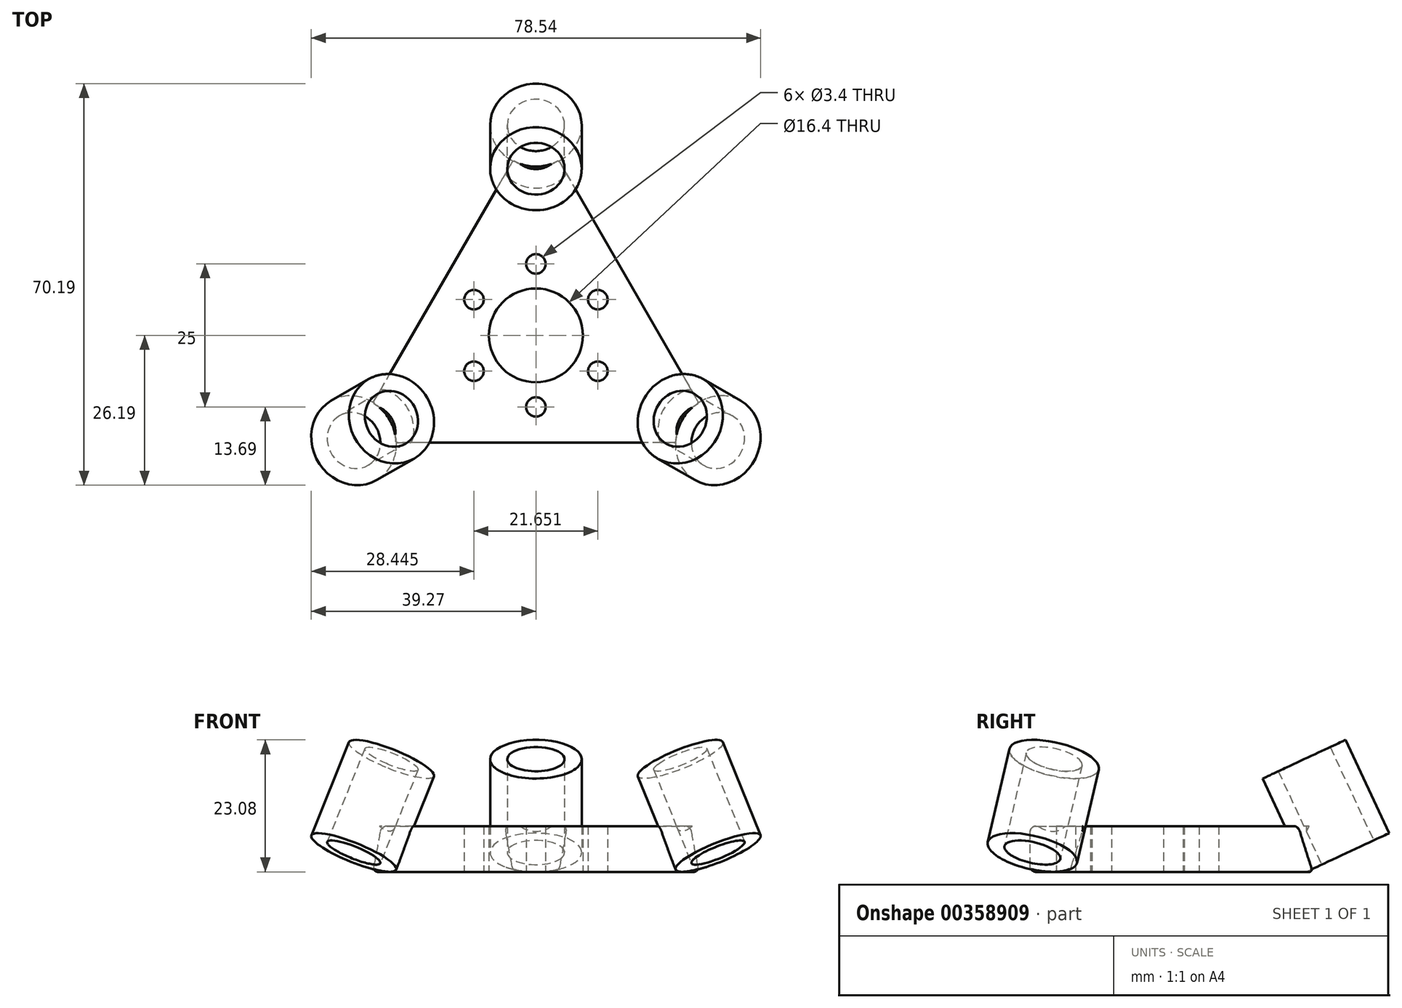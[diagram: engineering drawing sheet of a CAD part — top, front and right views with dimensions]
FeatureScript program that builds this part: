
annotation { "Feature Type Name" : "Feature", "Feature Type Description" : "" }
export const myFeature = defineFeature(function(context is Context, id is Id, definition is map)
    precondition{}
    {
        {
            var Q0;
            Q0=qCreatedBy(makeId("Top.planeOp"),FACE);
            var sketch = newSketch(context, id + "F0", { "sketchPlane" : qUnion([Q0])});
            skCircle(sketch, "E0.cCircle", {"center": v(0, 0) * mm, "radius": 37.5 * mm, "construction": true});
            skLineSegment(sketch, "E0.0", {"start": v(32.48, -18.75) * mm, "end": v(-32.48, -18.75) * mm});
            skLineSegment(sketch, "E0.1", {"start": v(-32.48, -18.75) * mm, "end": v(0, 37.5) * mm});
            skLineSegment(sketch, "E0.2", {"start": v(0, 37.5) * mm, "end": v(32.48, -18.75) * mm});
            skPoint(sketch, "E1.2.0", {"position": v(32.48, -18.75) * mm});
            skPoint(sketch, "E1.center", {"position": v(0, -0.05) * mm});
            skCircle(sketch, "E2", {"center": v(0, 0) * mm, "radius": 8.2 * mm});
            skCircle(sketch, "E3", {"center": v(0, 37.5) * mm, "radius": 8 * mm});
            skLineSegment(sketch, "E4", {"start": v(0, 37.5) * mm, "end": v(0, 29.5) * mm, "construction": true});
            skCircle(sketch, "E5.1.0", {"center": v(-32.48, -18.75) * mm, "radius": 8 * mm});
            skCircle(sketch, "E5.2.0", {"center": v(32.48, -18.75) * mm, "radius": 8 * mm});
            skCircle(sketch, "E6", {"center": v(0, 37.5) * mm, "radius": 5 * mm});
            skCircle(sketch, "E7", {"center": v(0, 12.5) * mm, "radius": 1.7 * mm});
            skCircle(sketch, "E8.1.0", {"center": v(-10.83, 6.25) * mm, "radius": 1.7 * mm});
            skCircle(sketch, "E8.2.0", {"center": v(-10.83, -6.25) * mm, "radius": 1.7 * mm});
            skCircle(sketch, "E8.3.0", {"center": v(0, -12.5) * mm, "radius": 1.7 * mm});
            skCircle(sketch, "E8.4.0", {"center": v(10.83, -6.25) * mm, "radius": 1.7 * mm});
            skCircle(sketch, "E8.5.0", {"center": v(10.83, 6.25) * mm, "radius": 1.7 * mm});
            skSolve(sketch);
        }
        {
            var Q0;
            Q0=makeQuery(id+"F0.imprint","IMPRINT",FACE,{"disambiguationData":[TD([[makeQuery(id+"F0.imprint","IMPRINT",EDGE,{"derivedFrom":sQuery(id+"F0.wireOp",EDGE,"E2")}),-1.0]])]});
            extrude(context, id + "F1", {"entities" : qUnion([Q0]), "depth" : 8 * mm});
        }
        {
            var Q0;
            {var subQ0=sQuery(id+"F0.wireOp",EDGE,"E3");var subQ1=sQuery(id+"F0.wireOp",EDGE,"E0.1");var subQ2=makeQuery(id+"F0.imprint","INTERSECT",VERTEX,{"derivedFrom":[subQ1,subQ0]});Q0=makeQuery(id+"F0.imprint","IMPRINT",FACE,{"disambiguationData":[TD([[makeQuery(id+"F0.imprint","IMPRINT",EDGE,{"disambiguationData":[TD([[subQ2,-1.0]])],"derivedFrom":subQ1}),1.0]])]});}
            var Q1;
            {var subQ0=sQuery(id+"F0.wireOp",EDGE,"E3");var subQ1=sQuery(id+"F0.wireOp",EDGE,"E0.1");var subQ2=makeQuery(id+"F0.imprint","INTERSECT",VERTEX,{"derivedFrom":[subQ1,subQ0]});Q1=makeQuery(id+"F0.imprint","IMPRINT",FACE,{"disambiguationData":[TD([[makeQuery(id+"F0.imprint","IMPRINT",EDGE,{"disambiguationData":[TD([[subQ2,-1.0]])],"derivedFrom":subQ1}),-1.0]])]});}
            extrude(context, id + "F2", {"entities" : qUnion([Q0, Q1]), "depth" : 18 * mm});
        }
        {
            var Q0;
            Q0=makeQuery(id+"F2.opExtrude","SWEPT_BODY",BODY,{"disambiguationData":[OSD([sQuery(id+"F0.wireOp",EDGE,"E3")])]});
            var Q1;
            Q1=makeQuery(id+"F2.opExtrude","SWEPT_FACE",FACE,{"disambiguationData":[OSD([sQuery(id+"F0.wireOp",EDGE,"E3")])]});
            transform(context, id + "F3", {"entities" : qUnion([Q0]), "transformType" : TransformType.ROTATION, "transformAxis" : qUnion([Q1]), "angle" : 25 * degree, "makeCopy" : false});
        }
        {
            var Q0;
            Q0=qCreatedBy(makeId("Right.planeOp"),FACE);
            var sketch = newSketch(context, id + "F4", { "sketchPlane" : qUnion([Q0])});
            skCircle(sketch, "E9", {"center": v(29.5, 0) * mm, "radius": 8 * mm, "construction": true});
            skSolve(sketch);
        }
        {
            var Q0;
            Q0=makeQuery(id+"F2.opExtrude","SWEPT_BODY",BODY,{"disambiguationData":[OSD([sQuery(id+"F0.wireOp",EDGE,"E3")])]});
            var Q1;
            Q1=sQuery(id+"F4.wireOp",EDGE,"E9");
            transform(context, id + "F5", {"entities" : qUnion([Q0]), "transformType" : TransformType.ROTATION, "transformAxis" : qUnion([Q1]), "angle" : 25 * degree, "makeCopy" : false});
        }
        {
            var Q0;
            Q0=makeQuery(id+"F2.opExtrude","SWEPT_BODY",BODY,{"disambiguationData":[OSD([sQuery(id+"F0.wireOp",EDGE,"E3")])]});
            var Q1;
            Q1=sQuery(id+"F0.wireOp",EDGE,"E0.cCircle");
            circularPattern(context, id + "F6", {"operationType" : NewBodyOperationType.ADD, "entities" : qUnion([Q0]), "axis" : qUnion([Q1]), "angle" : 360 * degree, "instanceCount" : 3, "equalSpace" : true});
        }
        {
            var Q0;
            Q0=makeQuery(id+"F1.opExtrude","CAP_EDGE",EDGE,{"disambiguationData":[OSD([sQuery(id+"F0.wireOp",EDGE,"E0.2")])],"isStart":false});
            var Q1;
            Q1=makeQuery(id+"F1.opExtrude","CAP_EDGE",EDGE,{"disambiguationData":[OSD([sQuery(id+"F0.wireOp",EDGE,"E0.2")])],"isStart":true});
            var Q2;
            Q2=makeQuery(id+"F1.opExtrude","CAP_EDGE",EDGE,{"disambiguationData":[OSD([sQuery(id+"F0.wireOp",EDGE,"E0.0")])],"isStart":false});
            var Q3;
            Q3=makeQuery(id+"F1.opExtrude","CAP_EDGE",EDGE,{"disambiguationData":[OSD([sQuery(id+"F0.wireOp",EDGE,"E0.1")])],"isStart":false});
            var Q4;
            Q4=makeQuery(id+"F1.opExtrude","CAP_EDGE",EDGE,{"disambiguationData":[OSD([sQuery(id+"F0.wireOp",EDGE,"E0.1")])],"isStart":true});
            var Q5;
            Q5=makeQuery(id+"F1.opExtrude","CAP_EDGE",EDGE,{"disambiguationData":[OSD([sQuery(id+"F0.wireOp",EDGE,"E0.0")])],"isStart":true});
            fillet(context, id + "F7", {"entities" : qUnion([Q0, Q1, Q2, Q3, Q4, Q5]), "radius" : 1 * mm, "tangentPropagation" : true, "allowEdgeOverflow" : false});
        }
    });
